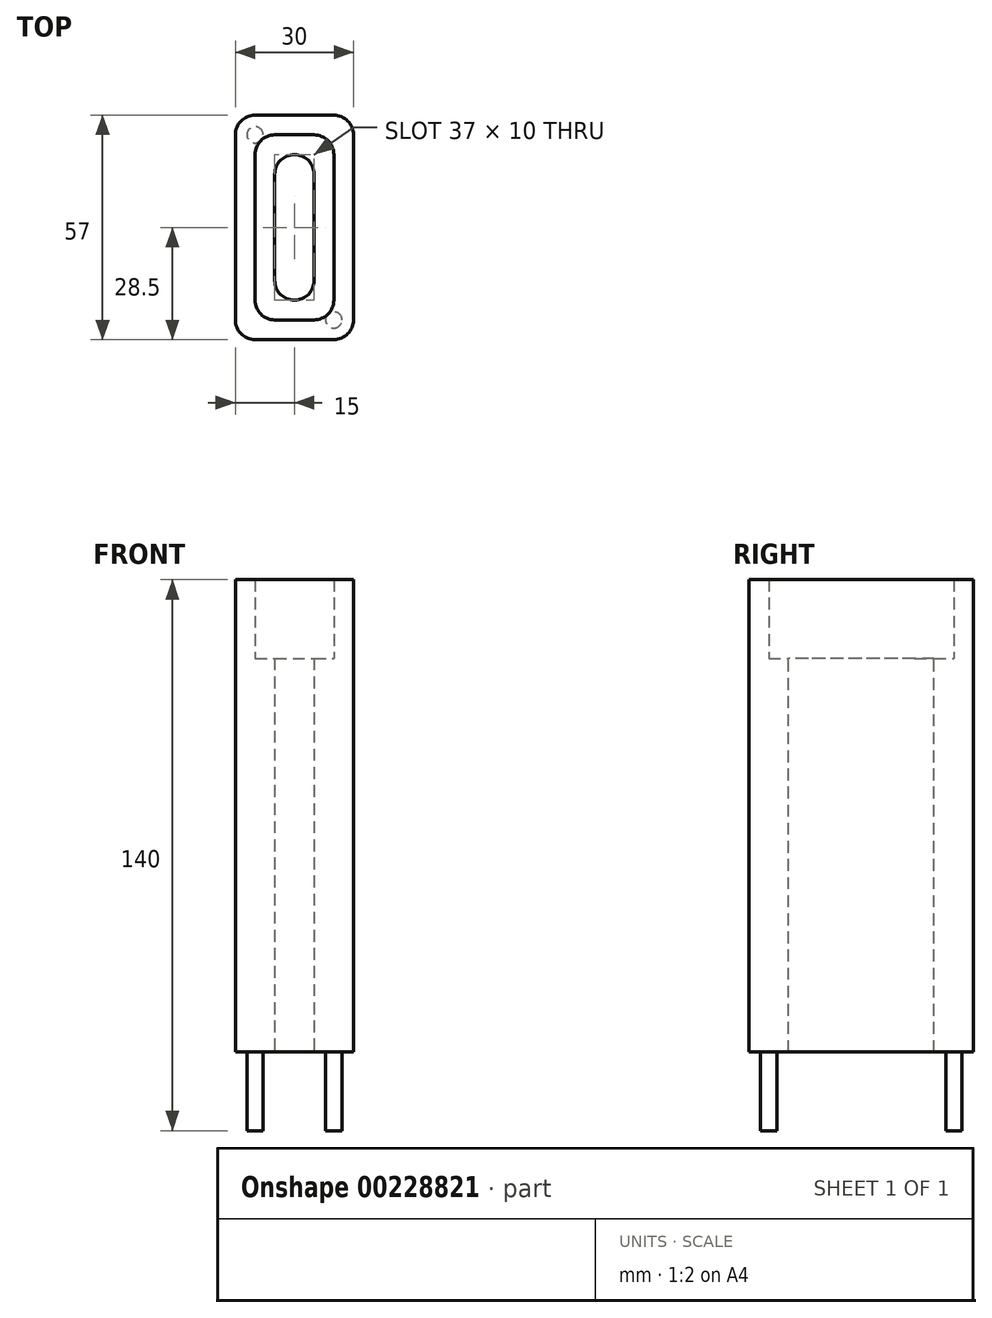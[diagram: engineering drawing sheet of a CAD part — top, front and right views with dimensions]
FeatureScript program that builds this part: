
annotation { "Feature Type Name" : "Feature", "Feature Type Description" : "" }
export const myFeature = defineFeature(function(context is Context, id is Id, definition is map)
    precondition{}
    {
        {
            var Q0;
            Q0=qCreatedBy(makeId("Top.planeOp"),FACE);
            var sketch = newSketch(context, id + "F0", { "sketchPlane" : qUnion([Q0])});
            skLineSegment(sketch, "E0.bottom", {"start": v(-10, 23.5) * mm, "end": v(10, 23.5) * mm});
            skLineSegment(sketch, "E0.top", {"start": v(-10, -23.5) * mm, "end": v(10, -23.5) * mm});
            skLineSegment(sketch, "E0.left", {"start": v(-10, 23.5) * mm, "end": v(-10, -23.5) * mm});
            skLineSegment(sketch, "E0.right", {"start": v(10, 23.5) * mm, "end": v(10, -23.5) * mm});
            skLineSegment(sketch, "E1.0", {"start": v(-15, 28.5) * mm, "end": v(15, 28.5) * mm});
            skLineSegment(sketch, "E1.1", {"start": v(-15, 28.5) * mm, "end": v(-15, -28.5) * mm});
            skLineSegment(sketch, "E1.2", {"start": v(-15, -28.5) * mm, "end": v(15, -28.5) * mm});
            skLineSegment(sketch, "E1.3", {"start": v(15, 28.5) * mm, "end": v(15, -28.5) * mm});
            skSolve(sketch);
        }
        {
            var Q0;
            Q0=makeQuery(id+"F0.imprint","IMPRINT",FACE,{"disambiguationData":[TD([[makeQuery(id+"F0.imprint","IMPRINT",EDGE,{"derivedFrom":sQuery(id+"F0.wireOp",EDGE,"E0.bottom")}),1.0]])]});
            extrude(context, id + "F1", {"entities" : qUnion([Q0]), "depth" : 70 * mm, "hasSecondDirection" : true, "secondDirectionOppositeDirection" : true, "secondDirectionDepth" : 70 * mm});
        }
        {
            var Q0;
            Q0=makeQuery(id+"F1.opExtrude","SWEPT_EDGE",EDGE,{"disambiguationData":[OSD([sQuery(id+"F0.wireOp",EDGE,"E0.bottom"),sQuery(id+"F0.wireOp",EDGE,"E0.left")])]});
            var Q1;
            Q1=makeQuery(id+"F1.opExtrude","SWEPT_EDGE",EDGE,{"disambiguationData":[OSD([sQuery(id+"F0.wireOp",EDGE,"E0.bottom"),sQuery(id+"F0.wireOp",EDGE,"E0.right")])]});
            var Q2;
            Q2=makeQuery(id+"F1.opExtrude","SWEPT_EDGE",EDGE,{"disambiguationData":[OSD([sQuery(id+"F0.wireOp",EDGE,"E0.top"),sQuery(id+"F0.wireOp",EDGE,"E0.left")])]});
            var Q3;
            Q3=makeQuery(id+"F1.opExtrude","SWEPT_EDGE",EDGE,{"disambiguationData":[OSD([sQuery(id+"F0.wireOp",EDGE,"E0.top"),sQuery(id+"F0.wireOp",EDGE,"E0.right")])]});
            var Q4;
            Q4=makeQuery(id+"F1.opExtrude","SWEPT_EDGE",EDGE,{"disambiguationData":[OSD([sQuery(id+"F0.wireOp",EDGE,"E1.0"),sQuery(id+"F0.wireOp",EDGE,"E1.1")])]});
            var Q5;
            Q5=makeQuery(id+"F1.opExtrude","SWEPT_EDGE",EDGE,{"disambiguationData":[OSD([sQuery(id+"F0.wireOp",EDGE,"E1.0"),sQuery(id+"F0.wireOp",EDGE,"E1.3")])]});
            var Q6;
            Q6=makeQuery(id+"F1.opExtrude","SWEPT_EDGE",EDGE,{"disambiguationData":[OSD([sQuery(id+"F0.wireOp",EDGE,"E1.2"),sQuery(id+"F0.wireOp",EDGE,"E1.3")])]});
            var Q7;
            Q7=makeQuery(id+"F1.opExtrude","SWEPT_EDGE",EDGE,{"disambiguationData":[OSD([sQuery(id+"F0.wireOp",EDGE,"E1.1"),sQuery(id+"F0.wireOp",EDGE,"E1.2")])]});
            fillet(context, id + "F2", {"entities" : qUnion([Q0, Q1, Q2, Q3, Q4, Q5, Q6, Q7]), "radius" : 5 * mm, "tangentPropagation" : true, "allowEdgeOverflow" : false});
        }
        {
            var Q0;
            Q0=makeQuery(id+"F1.opExtrude","CAP_FACE",FACE,{"disambiguationData":[OSD([sQuery(id+"F0.wireOp",EDGE,"E0.bottom"),sQuery(id+"F0.wireOp",EDGE,"E0.top"),sQuery(id+"F0.wireOp",EDGE,"E0.left"),sQuery(id+"F0.wireOp",EDGE,"E0.right"),sQuery(id+"F0.wireOp",EDGE,"E1.0"),sQuery(id+"F0.wireOp",EDGE,"E1.1"),sQuery(id+"F0.wireOp",EDGE,"E1.2"),sQuery(id+"F0.wireOp",EDGE,"E1.3")])],"isStart":true});
            var sketch = newSketch(context, id + "F3", { "sketchPlane" : qUnion([Q0])});
            skLineSegment(sketch, "E2.0", {"start": v(-5, 18.5) * mm, "end": v(5, 18.5) * mm});
            skLineSegment(sketch, "E2.1", {"start": v(-5, -18.5) * mm, "end": v(-5, 18.5) * mm});
            skLineSegment(sketch, "E2.2", {"start": v(-5, -18.5) * mm, "end": v(5, -18.5) * mm});
            skLineSegment(sketch, "E2.3", {"start": v(5, -18.5) * mm, "end": v(5, 18.5) * mm});
            skSolve(sketch);
        }
        {
            var Q0;
            Q0=makeQuery(id+"F3.imprint","IMPRINT",FACE,{"disambiguationData":[TD([[makeQuery(id+"F3.imprint","IMPRINT",EDGE,{"derivedFrom":sQuery(id+"F3.wireOp",EDGE,"E2.0")}),1.0]])]});
            extrude(context, id + "F4", {"entities" : qUnion([Q0]), "operationType" : NewBodyOperationType.ADD, "oppositeDirection" : true, "depth" : 120 * mm});
        }
        {
            var Q0;
            Q0=makeQuery(id+"F4.opExtrude","SWEPT_EDGE",EDGE,{"disambiguationData":[OSD([sQuery(id+"F3.wireOp",EDGE,"E2.0"),sQuery(id+"F3.wireOp",EDGE,"E2.1")])]});
            var Q1;
            Q1=makeQuery(id+"F4.opExtrude","SWEPT_EDGE",EDGE,{"disambiguationData":[OSD([sQuery(id+"F3.wireOp",EDGE,"E2.0"),sQuery(id+"F3.wireOp",EDGE,"E2.3")])]});
            var Q2;
            Q2=makeQuery(id+"F4.opExtrude","SWEPT_EDGE",EDGE,{"disambiguationData":[OSD([sQuery(id+"F3.wireOp",EDGE,"E2.2"),sQuery(id+"F3.wireOp",EDGE,"E2.3")])]});
            var Q3;
            Q3=makeQuery(id+"F4.opExtrude","SWEPT_EDGE",EDGE,{"disambiguationData":[OSD([sQuery(id+"F3.wireOp",EDGE,"E2.1"),sQuery(id+"F3.wireOp",EDGE,"E2.2")])]});
            fillet(context, id + "F5", {"entities" : qUnion([Q0, Q1, Q2, Q3]), "radius" : 5 * mm, "tangentPropagation" : true, "allowEdgeOverflow" : false});
        }
        {
            var Q0;
            {var subQ0=sQuery(id+"F0.wireOp",EDGE,"E1.3");var subQ1=sQuery(id+"F0.wireOp",EDGE,"E1.2");var subQ2=sQuery(id+"F0.wireOp",EDGE,"E1.1");var subQ3=sQuery(id+"F0.wireOp",EDGE,"E1.0");var subQ4=sQuery(id+"F0.wireOp",EDGE,"E0.right");var subQ5=sQuery(id+"F0.wireOp",EDGE,"E0.left");var subQ6=sQuery(id+"F0.wireOp",EDGE,"E0.top");var subQ7=sQuery(id+"F0.wireOp",EDGE,"E0.bottom");Q0=makeQuery(id+"F4.boolean.opBoolean","MERGE",FACE,{"derivedFrom":[makeQuery(id+"F1.opExtrude","CAP_FACE",FACE,{"disambiguationData":[OSD([subQ7,subQ6,subQ5,subQ4,subQ3,subQ2,subQ1,subQ0])],"isStart":true}),makeQuery(id+"F4.opExtrude","CAP_FACE",FACE,{"disambiguationData":[OSD([subQ7,subQ6,subQ5,subQ4,subQ3,subQ2,subQ1,subQ0,sQuery(id+"F3.wireOp",EDGE,"E2.0"),sQuery(id+"F3.wireOp",EDGE,"E2.1"),sQuery(id+"F3.wireOp",EDGE,"E2.2"),sQuery(id+"F3.wireOp",EDGE,"E2.3")])],"isStart":true})]});}
            var sketch = newSketch(context, id + "F6", { "sketchPlane" : qUnion([Q0])});
            skCircle(sketch, "E3", {"center": v(-10, 23.5) * mm, "radius": 2.07 * mm});
            skCircle(sketch, "E4.MirrorC", {"center": v(10, 23.5) * mm, "radius": 2.07 * mm});
            skCircle(sketch, "E5.MirrorC", {"center": v(-10, -23.5) * mm, "radius": 2.07 * mm});
            skCircle(sketch, "E6.MirrorC", {"center": v(10, -23.5) * mm, "radius": 2.07 * mm});
            skSolve(sketch);
        }
        {
            var Q0;
            Q0=makeQuery(id+"F6.imprint","IMPRINT",FACE,{"disambiguationData":[TD([[makeQuery(id+"F6.imprint","IMPRINT",EDGE,{"derivedFrom":sQuery(id+"F6.wireOp",EDGE,"E3")}),1.0]])]});
            var Q1;
            Q1=makeQuery(id+"F6.imprint","IMPRINT",FACE,{"disambiguationData":[TD([[makeQuery(id+"F6.imprint","IMPRINT",EDGE,{"derivedFrom":sQuery(id+"F6.wireOp",EDGE,"E4.MirrorC")}),-1.0]])]});
            var Q2;
            Q2=makeQuery(id+"F6.imprint","IMPRINT",FACE,{"disambiguationData":[TD([[makeQuery(id+"F6.imprint","IMPRINT",EDGE,{"derivedFrom":sQuery(id+"F6.wireOp",EDGE,"E5.MirrorC")}),-1.0]])]});
            var Q3;
            Q3=makeQuery(id+"F6.imprint","IMPRINT",FACE,{"disambiguationData":[TD([[makeQuery(id+"F6.imprint","IMPRINT",EDGE,{"derivedFrom":sQuery(id+"F6.wireOp",EDGE,"E6.MirrorC")}),1.0]])]});
            extrude(context, id + "F7", {"entities" : qUnion([Q0, Q1, Q2, Q3]), "operationType" : NewBodyOperationType.REMOVE, "oppositeDirection" : true, "depth" : 20 * mm});
        }
    });
